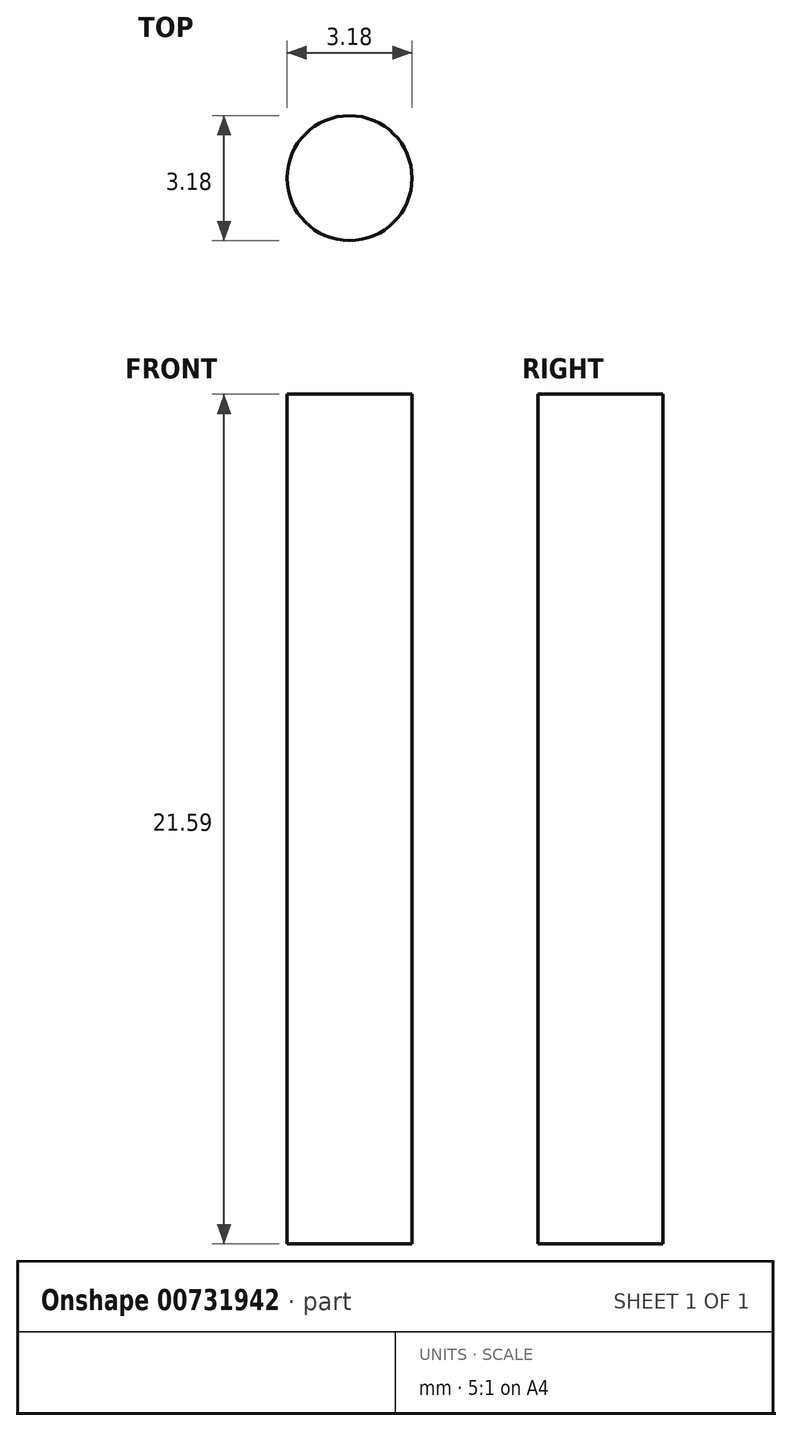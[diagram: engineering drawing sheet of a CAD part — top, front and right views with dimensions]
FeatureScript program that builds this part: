
annotation { "Feature Type Name" : "Feature", "Feature Type Description" : "" }
export const myFeature = defineFeature(function(context is Context, id is Id, definition is map)
    precondition{}
    {
        {
            var Q0;
            Q0=qCreatedBy(makeId("Top.planeOp"),FACE);
            var sketch = newSketch(context, id + "F0", { "sketchPlane" : qUnion([Q0])});
            skCircle(sketch, "E0", {"center": v(0, 0) * mm, "radius": 1.59 * mm});
            skSolve(sketch);
        }
        {
            var Q0;
            Q0=makeQuery(id+"F0.imprint","IMPRINT",FACE,{"disambiguationData":[TD([[makeQuery(id+"F0.imprint","IMPRINT",EDGE,{"derivedFrom":sQuery(id+"F0.wireOp",EDGE,"E0")}),1.0]])]});
            extrude(context, id + "F1", {"entities" : qUnion([Q0]), "depth" : 21.59 * mm, "offsetDistance" : 25.4 * mm});
        }
    });
